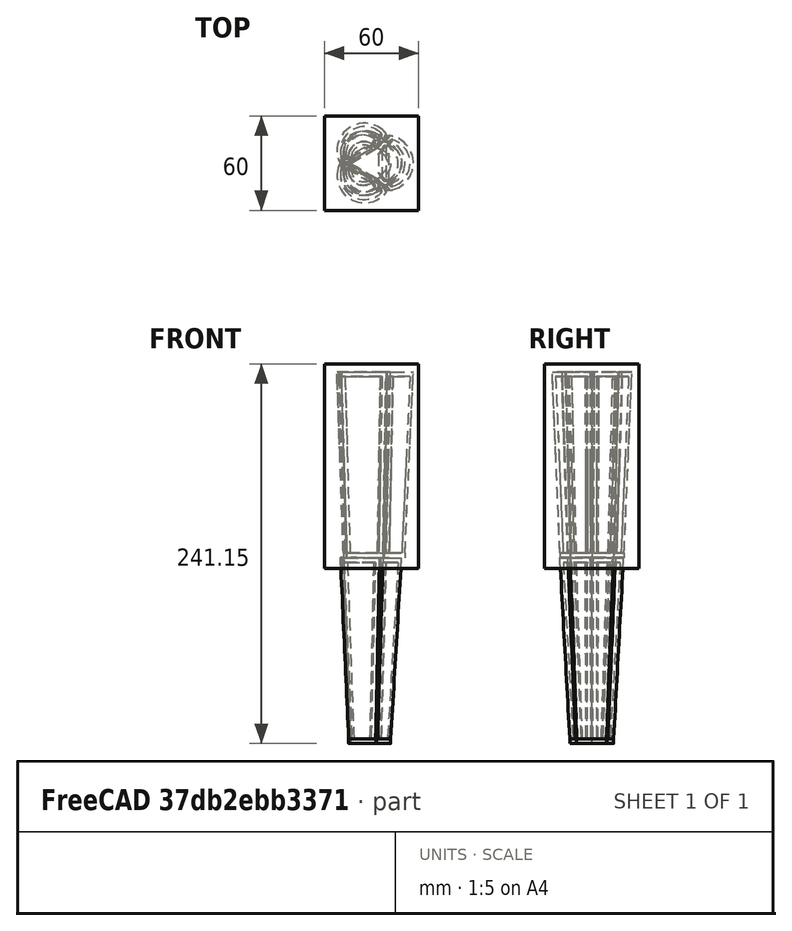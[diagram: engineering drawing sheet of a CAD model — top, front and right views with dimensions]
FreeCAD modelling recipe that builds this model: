
FCSTD DOCUMENT  (FreeCAD 0.18.4R)
Label: GeometriesAligned
License: All rights reserved
LicenseURL: http://en.wikipedia.org/wiki/All_rights_reserved
objects: Part::FeaturePython×6, Sketcher::SketchObject×3, Part::Feature×2, Part::Box×2, App::DocumentObjectGroup×1, Part::Cut×1, Part::MultiCommon×1, Part::MultiFuse×1, PartDesign::Body×1
note: 17 computed .brp shape members not serialized (recipe doc carries the construction recipe); baked Part::Feature solids carry a one-line shape summary decoded from their .brp

FEATURE [Part::Feature] Part__Feature  label="non-groove-segment1"
  Placement = pos=(16,26,-210) rot=(1,0,0;1.5708rad)
  shape: bbox 38.93 x 40.62 x 124.8 mm, 69 faces (baked)
FEATURE [Part::Feature] Part__Feature001  label="non-groove-segment002"
  Placement = pos=(18,26.25,-92) rot=(1,0,0;1.5708rad)
  shape: bbox 48.64 x 50.76 x 124.7 mm, 73 faces (baked)
FEATURE [Sketcher::SketchObject] Sketch
  MapMode = 5
  Placement = pos=(0,0,0) rot=(0.57735,0.57735,0.57735;2.0944rad)
  Support = -> [YZ_Plane]
  sketch-geometry (3):
    g0: GeomPoint X=-25 Y=92 Z=0
    g1: LineSegment StartX=-26 StartY=5 StartZ=0 EndX=26 EndY=5 EndZ=0
    g2: LineSegment StartX=18.1432 StartY=0 StartZ=0 EndX=18.1432 EndY=-118.5 EndZ=0
  constraints (9):
    c: DistanceY(g-1,g0) = 92
    c: DistanceX(g0,g-1) = 25
    c: Horizontal(g1)
    c: DistanceX(g1,g1) = 52
    c: DistanceX(g1,g-1) = 26
    c: DistanceY(g-1,g1) = 5
    c: Vertical(g2)
    c: PointOnObject(g2,g-1)
    c: DistanceY(g2,g2) = 118.5
FEATURE [Part::Box] Box  label="Cube"
  AttacherType = Attacher::AttachEngine3D
  Height = 130
  Length = 60
  Placement = pos=(-30,-30,-125) rot=(0,0,1;0rad)
  Width = 60
FEATURE [Part::FeaturePython] Slice  # WARN: FeaturePython — macro-defined, semantics opaque (R4)
  Base = -> Box
  Mode = 1
  Tolerance = 0
  Tools = -> [Part__Feature001]
FEATURE [Part::FeaturePython] Slice_child0  label="Slice.0"  # WARN: FeaturePython — macro-defined, semantics opaque (R4)
  Base = -> Slice
  FilterType = 1
  Invert = false
  OverrideMaxVal = 0
  WindowFrom = 80
  WindowTo = 100
  items = 0
FEATURE [Part::FeaturePython] Slice_child1  label="Slice.1"  # WARN: FeaturePython — macro-defined, semantics opaque (R4)
  Base = -> Slice
  FilterType = 1
  Invert = false
  OverrideMaxVal = 0
  WindowFrom = 80
  WindowTo = 100
  items = 1
FEATURE [Part::FeaturePython] Slice_child2  label="Slice.2"  # WARN: FeaturePython — macro-defined, semantics opaque (R4)
  Base = -> Slice
  FilterType = 1
  Invert = false
  OverrideMaxVal = 0
  WindowFrom = 80
  WindowTo = 100
  items = 2
FEATURE [Part::FeaturePython] Slice_child3  label="Slice.3"  # WARN: FeaturePython — macro-defined, semantics opaque (R4)
  Base = -> Slice
  FilterType = 1
  Invert = false
  OverrideMaxVal = 0
  WindowFrom = 80
  WindowTo = 100
  items = 3
FEATURE [Part::FeaturePython] Slice_child4  label="Slice.4"  # WARN: FeaturePython — macro-defined, semantics opaque (R4)
  Base = -> Slice
  FilterType = 1
  Invert = false
  OverrideMaxVal = 0
  WindowFrom = 80
  WindowTo = 100
  items = 4
FEATURE [App::DocumentObjectGroup] GrExplode_Slice  label="Exploded Slice"
  Group = -> [Slice_child0,Slice_child1,Slice_child2,Slice_child3,Slice_child4]
FEATURE [Part::Box] Box001  label="Cube001"
  AttacherType = Attacher::AttachEngine3D
  Height = 60
  Length = 60
  Placement = pos=(-30,-30,-55) rot=(0,0,1;0rad)
  Width = 60
FEATURE [Part::Cut] Cut
  Base = -> Part__Feature001
  Tool = -> Box001
FEATURE [Part::MultiCommon] Common
  Shapes = -> [Box001,Part__Feature001]
FEATURE [Part::MultiFuse] Fusion
  Shapes = -> [Common,Cut]
FEATURE [Sketcher::SketchObject] Sketch001
  MapMode = 5
  Support = -> [XY_Plane]
  sketch-geometry (10):
    g0: LineSegment StartX=10 StartY=15 StartZ=0 EndX=19 EndY=10 EndZ=0
    g1: LineSegment StartX=19 StartY=10 StartZ=0 EndX=21.5 EndY=5 EndZ=0
    g2: LineSegment StartX=21.5 StartY=5 StartZ=0 EndX=22.5 EndY=0 EndZ=0
    g3: LineSegment StartX=22.5 StartY=0 StartZ=0 EndX=21.8437 EndY=-4.99813 EndZ=0
    g4: LineSegment StartX=21.8437 StartY=-4.99813 StartZ=0 EndX=17.7378 EndY=-11.2651 EndZ=0
    g5: LineSegment StartX=17.7378 StartY=-11.2651 StartZ=0 EndX=10 EndY=-15.3671 EndZ=0
    g6: LineSegment StartX=10 StartY=-15.3671 StartZ=0 EndX=10 EndY=15 EndZ=0
    g7: LineSegment StartX=0 StartY=0 StartZ=0 EndX=-13 EndY=-22.5167 EndZ=0
    g8: LineSegment StartX=0 StartY=0 StartZ=0 EndX=-13 EndY=22.5167 EndZ=0
    g9: LineSegment StartX=26 StartY=0 StartZ=0 EndX=0 EndY=0 EndZ=0
  constraints (25):
    c: Coincident(g0,g1)
    c: Coincident(g1,g2)
    c: Coincident(g2,g3)
    c: Coincident(g3,g4)
    c: Coincident(g4,g5)
    c: Coincident(g5,g6)
    c: Coincident(g6,g0)
    c: DistanceX(g-1,g2) = 22.5
    c: PointOnObject(g2,g-1)
    c: DistanceX(g-1,g1) = 21.5
    c: DistanceY(g-1,g0) = 15
    c: DistanceY(g-1,g1) = 5
    c: DistanceY(g-1,g0) = 10
    c: DistanceX(g0) = 19
    c: Vertical(g6)
    c: DistanceX(g-1,g0) = 10
    c: Coincident(g7,g-1)
    c: Angle(g7,g-1) = 2.0944
    c: Coincident(g8,g7)
    c: Angle(g-1,g8) = 2.0944
    c: Coincident(g9,g7)
    c: PointOnObject(g9,g-1)
    c: Equal(g7,g8)
    c: Equal(g8,g9)
    c: Distance(g7) = 26
FEATURE [Sketcher::SketchObject] Sketch002
  AttachmentOffset = pos=(0,0,0) rot=(0,0,1;-2.0944rad)
  MapMode = 5
  Placement = pos=(0,0,0) rot=(0,0,1;4.18879rad)
  Support = -> [XY_Plane]
  sketch-geometry (11):
    g0: LineSegment StartX=10 StartY=15 StartZ=0 EndX=19 EndY=10 EndZ=0
    g1: LineSegment StartX=19 StartY=10 StartZ=0 EndX=21.5 EndY=5 EndZ=0
    g2: LineSegment StartX=21.5 StartY=5 StartZ=0 EndX=22.5 EndY=0 EndZ=0
    g3: LineSegment StartX=22.5 StartY=0 StartZ=0 EndX=21.8437 EndY=-4.99813 EndZ=0
    g4: LineSegment StartX=21.8437 StartY=-4.99813 StartZ=0 EndX=17.7378 EndY=-11.2651 EndZ=0
    g5: LineSegment StartX=17.7378 StartY=-11.2651 StartZ=0 EndX=10 EndY=-15.3671 EndZ=0
    g6: LineSegment StartX=10 StartY=-15.3671 StartZ=0 EndX=10 EndY=15 EndZ=0
    g7: LineSegment StartX=-24.7655 StartY=24.8754 StartZ=0 EndX=26.1451 EndY=24.8754 EndZ=0
    g8: LineSegment StartX=26.1451 StartY=24.8754 StartZ=0 EndX=26.1451 EndY=-26.0351 EndZ=0
    g9: LineSegment StartX=26.1451 StartY=-26.0351 StartZ=0 EndX=-24.7655 EndY=-26.0351 EndZ=0
    g10: LineSegment StartX=-24.7655 StartY=-26.0351 StartZ=0 EndX=-24.7655 EndY=24.8754 EndZ=0
  constraints (25):
    c: Coincident(g0,g1)
    c: Coincident(g1,g2)
    c: Coincident(g2,g3)
    c: Coincident(g3,g4)
    c: Coincident(g4,g5)
    c: Coincident(g5,g6)
    c: Coincident(g6,g0)
    c: DistanceX(g-1,g2) = 22.5
    c: PointOnObject(g2,g-1)
    c: DistanceX(g-1,g1) = 21.5
    c: DistanceY(g-1,g0) = 15
    c: DistanceY(g-1,g1) = 5
    c: DistanceY(g-1,g0) = 10
    c: DistanceX(g0) = 19
    c: Vertical(g6)
    c: DistanceX(g-1,g0) = 10
    c: Coincident(g7,g8)
    c: Coincident(g8,g9)
    c: Coincident(g9,g10)
    c: Coincident(g10,g7)
    c: Horizontal(g7)
    c: Horizontal(g9)
    c: Vertical(g8)
    c: Vertical(g10)
    c: Equal(g7,g8)
FEATURE [PartDesign::Body] Body
  Group = -> [Sketch,Sketch001,Sketch002]
  Origin = -> Origin
